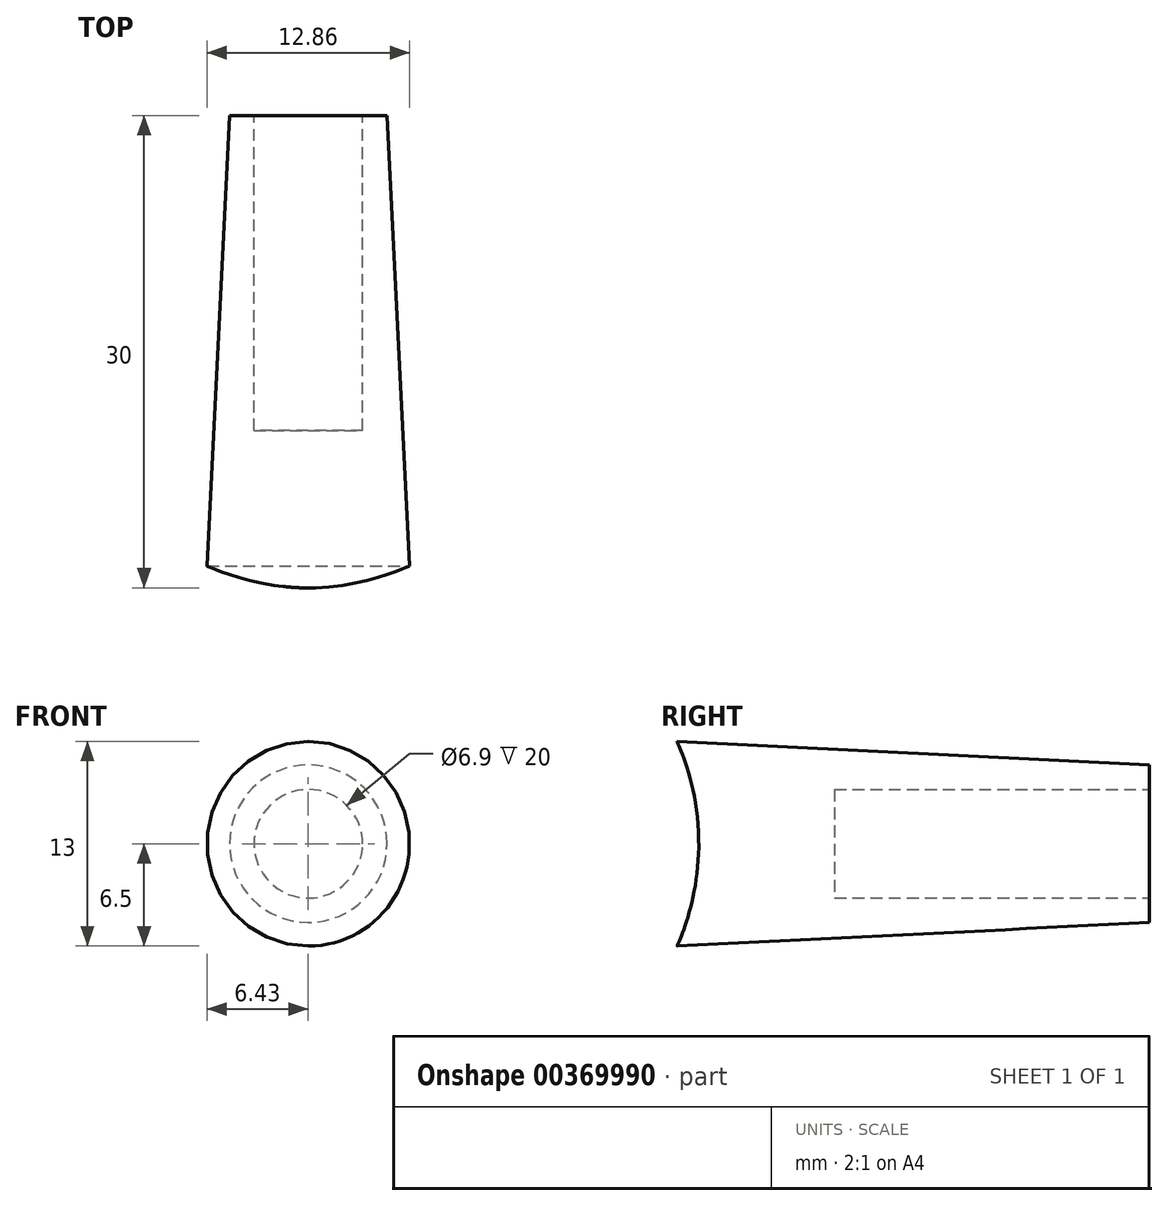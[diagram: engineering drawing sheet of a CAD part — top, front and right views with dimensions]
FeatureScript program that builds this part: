
annotation { "Feature Type Name" : "Feature", "Feature Type Description" : "" }
export const myFeature = defineFeature(function(context is Context, id is Id, definition is map)
    precondition{}
    {
        {
            var Q0;
            Q0=qCreatedBy(makeId("Front.planeOp"),FACE);
            var sketch = newSketch(context, id + "F0", { "sketchPlane" : qUnion([Q0])});
            skCircle(sketch, "E0", {"center": v(0, 0) * mm, "radius": 6.5 * mm});
            skSolve(sketch);
        }
        {
            var Q0;
            Q0=makeQuery(id+"F0.imprint","IMPRINT",FACE,{"disambiguationData":[TD([[makeQuery(id+"F0.imprint","IMPRINT",EDGE,{"derivedFrom":sQuery(id+"F0.wireOp",EDGE,"E0")}),1.0]])]});
            extrude(context, id + "F1", {"entities" : qUnion([Q0]), "depth" : 30 * mm});
        }
        {
            var Q0;
            Q0=qCreatedBy(makeId("Right.planeOp"),FACE);
            var sketch = newSketch(context, id + "F2", { "sketchPlane" : qUnion([Q0])});
            skCircle(sketch, "E1", {"center": v(-44.62, 0) * mm, "radius": 16 * mm});
            skPoint(sketch, "E2", {"position": v(-30, 6.5) * mm});
            skSolve(sketch);
        }
        {
            var Q0;
            Q0=makeQuery(id+"F2.imprint","IMPRINT",FACE,{"disambiguationData":[TD([[makeQuery(id+"F2.imprint","IMPRINT",EDGE,{"derivedFrom":sQuery(id+"F2.wireOp",EDGE,"E1")}),1.0]])]});
            extrude(context, id + "F3", {"entities" : qUnion([Q0]), "operationType" : NewBodyOperationType.REMOVE, "endBound" : BoundingType.THROUGH_ALL, "oppositeDirection" : true, "depth" : 25 * mm, "hasSecondDirection" : true, "secondDirectionOppositeDirection" : false, "secondDirectionDepth" : 25 * mm});
        }
        {
            var Q0;
            Q0=makeQuery(id+"F1.opExtrude","CAP_FACE",FACE,{"disambiguationData":[OSD([sQuery(id+"F0.wireOp",EDGE,"E0")])],"isStart":true});
            var sketch = newSketch(context, id + "F4", { "sketchPlane" : qUnion([Q0])});
            skCircle(sketch, "E3", {"center": v(0, 0) * mm, "radius": 3.45 * mm});
            skSolve(sketch);
        }
        {
            var Q0;
            Q0=makeQuery(id+"F4.imprint","IMPRINT",FACE,{"disambiguationData":[TD([[makeQuery(id+"F4.imprint","IMPRINT",EDGE,{"derivedFrom":sQuery(id+"F4.wireOp",EDGE,"E3")}),1.0]])]});
            extrude(context, id + "F5", {"entities" : qUnion([Q0]), "operationType" : NewBodyOperationType.REMOVE, "oppositeDirection" : true, "depth" : 20 * mm});
        }
        {
            var Q0;
            Q0=makeQuery(id+"F1.opExtrude","CAP_EDGE",EDGE,{"disambiguationData":[OSD([sQuery(id+"F0.wireOp",EDGE,"E0")])],"isStart":true});
            chamfer(context, id + "F6", {"entities" : qUnion([Q0]), "chamferType" : ChamferType.TWO_OFFSETS, "width1" : 30 * mm, "oppositeDirection" : false, "width2" : 1.5 * mm, "tangentPropagation" : true});
        }
    });
